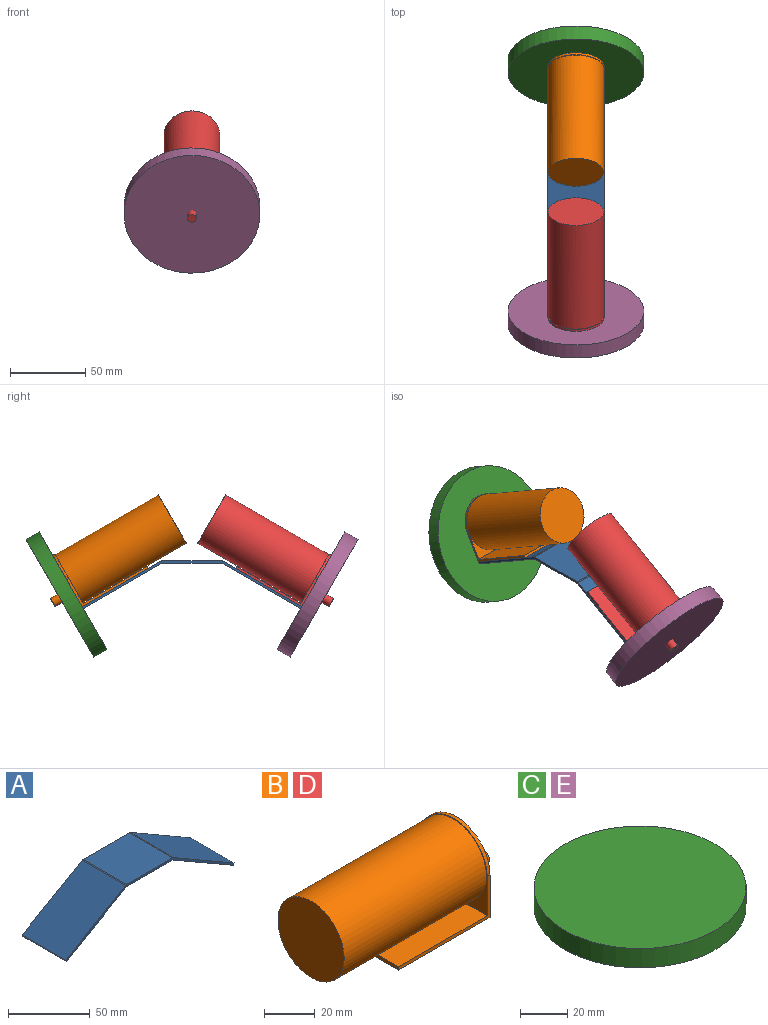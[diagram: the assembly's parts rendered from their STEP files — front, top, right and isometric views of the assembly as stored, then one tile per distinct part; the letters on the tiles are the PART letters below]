
ASSEMBLY  parts=5 mates=6
PART A: 12 faces, bbox 145.5x37.6x31.6 mm
  f0: plane 40x37.59mm, normal (0,0,1), area 1503.6mm2, adj f1,f9,f10,f11
  f1: cylinder r=1.59mm len=37.59mm, axis (0,1,0), area 31.3mm2, adj f0,f2,f10,f11
  f2: plane 51.96x37.59mm, normal (-0.5,0,0.87), area 2255.4mm2, adj f1,f3,f10,f11
  f3: plane 37.59x1.38mm, normal (-0.87,0,-0.5), area 59.8mm2, adj f2,f4,f10,f11
  f4: plane 51.96x37.59mm, normal (0.5,0,-0.87), area 2255.4mm2, adj f3,f5,f10,f11
  f5: plane 40x37.59mm, normal (0,0,-1), area 1503.6mm2, adj f4,f6,f10,f11
  f6: plane 51.96x37.59mm, normal (-0.5,0,-0.87), area 2255.4mm2, adj f5,f7,f10,f11
  f7: plane 37.59x1.38mm, normal (0.87,0,-0.5), area 59.8mm2, adj f6,f8,f10,f11
  f8: plane 51.96x37.59mm, normal (0.5,0,0.87), area 2255.4mm2, adj f7,f9,f10,f11
  f9: cylinder r=1.59mm len=37.59mm, axis (0,1,0), area 31.3mm2, adj f0,f8,f10,f11
  f10: plane 145.51x31.59mm, normal (0,-1,0), area 255.7mm2, adj f0,f1,f2,f3,f4,f5,f6,f7
  f11: plane 145.51x31.59mm, normal (0,1,0), area 255.7mm2, adj f0,f1,f2,f3,f4,f5,f6,f7
PART B: 12 faces, bbox 96.2x37.6x39.2 mm
  f0: plane 50.8x20.39mm, normal (0,1,0), area 110.7mm2, adj f1,f3,f4,f5,f6,f7
  f1: plane 37.59x1.59mm, normal (-1,0,0), area 59.8mm2, adj f0,f2,f4,f5
  f2: plane 50.8x20.39mm, normal (0,-1,0), area 110.7mm2, adj f1,f3,f4,f5,f6,f7
  f3: plane 39.18x37.59mm, normal (1,0,0), area 1292.9mm2, adj f0,f2,f5,f6,f10
  f4: plane 49.21x37.59mm, normal (0,0,1), area 1849.8mm2, adj f0,f1,f2,f7
  f5: plane 50.8x37.59mm, normal (0,0,-1), area 1909.6mm2, adj f0,f1,f2,f3
  f6: cylinder r=18.79mm len=37.59mm, axis (1,0,0), area 93.9mm2, adj f0,f2,f3,f7
  f7: plane 37.59x37.59mm, normal (-1,0,0), area 197.8mm2, adj f0,f2,f4,f6,f8
  f8: cylinder r=18.4mm len=79.1mm, axis (1,0,0), area 9144.8mm2, adj f7,f9
  f9: plane 36.8x36.8mm, normal (-1,0,0), area 1063.6mm2, adj f8
  f10: cylinder r=3mm len=15.5mm, axis (-1,0,0), area 292.2mm2, adj f3,f11
  f11: plane 6x6mm, normal (1,0,0), area 28.3mm2, adj f10
PART C: 3 faces, bbox 90x90x10 mm
  f0: cylinder r=45mm len=90mm, axis (0,0,-1), area 2827.4mm2, adj f1,f2
  f1: plane 90x90mm, normal (0,0,1), area 6361.7mm2, adj f0
  f2: plane 90x90mm, normal (0,0,-1), area 6361.7mm2, adj f0
PART D: same geometry as B
PART E: same geometry as C
PLACE A rot(axis=(0,0,1),90deg) t=(11.53,-1.31,-4.42)mm
PLACE B rot(axis=(-0.25,0.25,0.94),93.8deg) t=(49.12,71.45,-33.04)mm
PLACE C rot(axis=(1,0,0),60deg) t=(30.33,86.15,-27.58)mm
PLACE D rot(axis=(0.25,0.25,-0.94),93.8deg) t=(11.53,-74.07,-33.04)mm
PLACE E rot(axis=(-1,0,0),60deg) t=(30.33,-88.77,-27.58)mm
MATE planar B.f5 <-> A.f8  axis (0,-0.5,-0.87) through (11.53,49.45,-20.34)mm
MATE fastened D.f3 <-> A.f3  axis (0,-0.87,-0.5) through (30.33,-74.07,-33.04)mm
MATE planar A.f2 <-> D.f5  axis (0,-0.5,0.87) through (30.33,-48.09,-18.04)mm
MATE revolute E.f0 <-> D.f10  axis (0,0.87,0.5) through (30.33,-80.11,-22.58)mm
MATE revolute C.f0 <-> B.f10  axis (0,-0.87,0.5) through (30.33,77.49,-22.58)mm
MATE fastened B.f3 <-> A.f7  axis (0,0.87,-0.5) through (30.33,71.45,-33.04)mm
